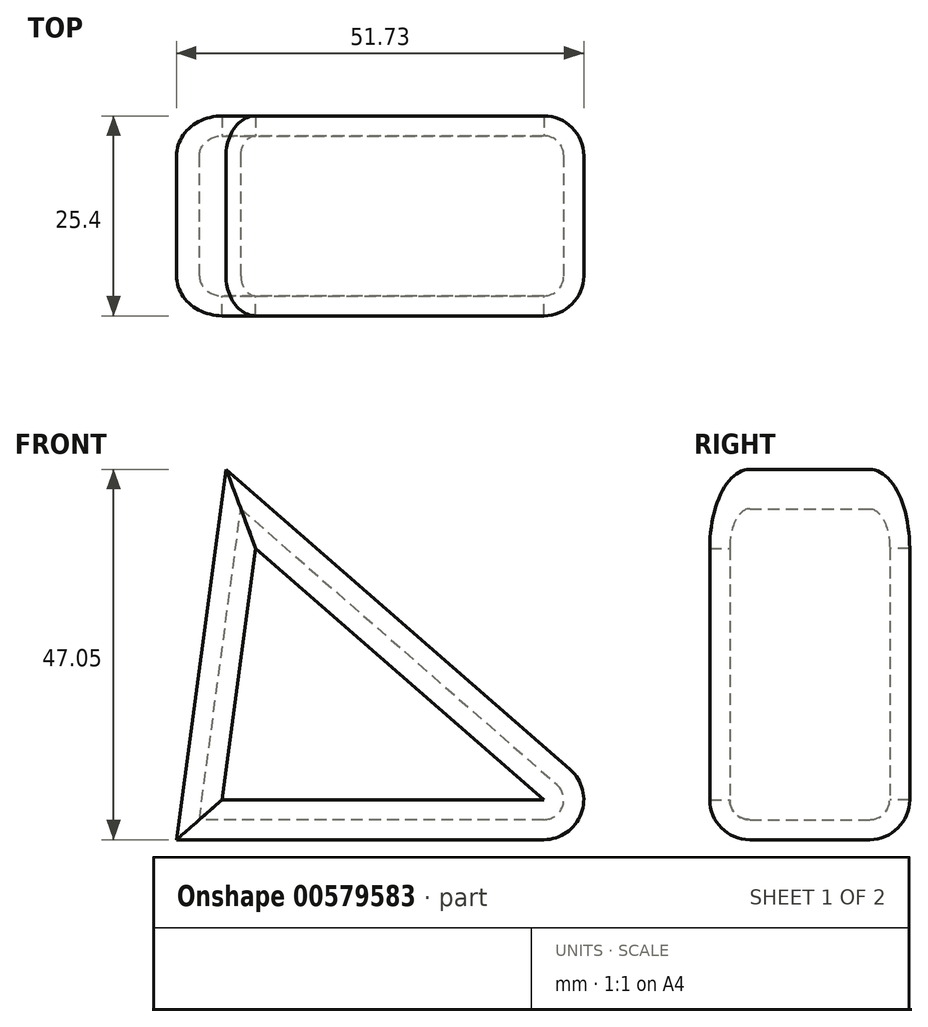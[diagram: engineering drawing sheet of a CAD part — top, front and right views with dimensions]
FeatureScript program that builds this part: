
annotation { "Feature Type Name" : "Feature", "Feature Type Description" : "" }
export const myFeature = defineFeature(function(context is Context, id is Id, definition is map)
    precondition{}
    {
        {
            var Q0;
            Q0=qCreatedBy(makeId("Front.planeOp"),FACE);
            var sketch = newSketch(context, id + "F0", { "sketchPlane" : qUnion([Q0])});
            skLineSegment(sketch, "E0", {"start": v(-18.29, 47.05) * mm, "end": v(35.62, 0) * mm});
            skLineSegment(sketch, "E1", {"start": v(35.62, 0) * mm, "end": v(-24.57, 0) * mm});
            skLineSegment(sketch, "E2", {"start": v(-24.57, 0) * mm, "end": v(-18.29, 47.05) * mm});
            skSolve(sketch);
        }
        {
            var Q0;
            Q0 = qSketchRegion(id + "F0", true);
            extrude(context, id + "F1", {"entities" : qUnion([Q0]), "depth" : 25.4 * mm, "offsetDistance" : 25.4 * mm});
        }
        {
            var Q0;
            Q0=makeQuery(id+"F1.opExtrude","CAP_EDGE",EDGE,{"disambiguationData":[OSD([sQuery(id+"F0.wireOp",EDGE,"E0")])],"isStart":false});
            var Q1;
            Q1=makeQuery(id+"F1.opExtrude","CAP_EDGE",EDGE,{"disambiguationData":[OSD([sQuery(id+"F0.wireOp",EDGE,"E2")])],"isStart":false});
            var Q2;
            Q2=makeQuery(id+"F1.opExtrude","CAP_EDGE",EDGE,{"disambiguationData":[OSD([sQuery(id+"F0.wireOp",EDGE,"E1")])],"isStart":false});
            var Q3;
            Q3=makeQuery(id+"F1.opExtrude","SWEPT_EDGE",EDGE,{"disambiguationData":[OSD([sQuery(id+"F0.wireOp",EDGE,"E0"),sQuery(id+"F0.wireOp",EDGE,"E1")])]});
            var Q4;
            Q4=makeQuery(id+"F1.opExtrude","CAP_EDGE",EDGE,{"disambiguationData":[OSD([sQuery(id+"F0.wireOp",EDGE,"E0")])],"isStart":true});
            var Q5;
            Q5=makeQuery(id+"F1.opExtrude","CAP_EDGE",EDGE,{"disambiguationData":[OSD([sQuery(id+"F0.wireOp",EDGE,"E2")])],"isStart":true});
            var Q6;
            Q6=makeQuery(id+"F1.opExtrude","CAP_EDGE",EDGE,{"disambiguationData":[OSD([sQuery(id+"F0.wireOp",EDGE,"E1")])],"isStart":true});
            fillet(context, id + "F2", {"entities" : qUnion([Q0, Q1, Q2, Q3, Q4, Q5, Q6]), "radius" : 5.08 * mm, "tangentPropagation" : true, "allowEdgeOverflow" : false});
        }
        {
            var Q0;
            Q0=makeQuery(id+"F1.opExtrude","CAP_FACE",FACE,{"disambiguationData":[OSD([sQuery(id+"F0.wireOp",EDGE,"E0"),sQuery(id+"F0.wireOp",EDGE,"E1"),sQuery(id+"F0.wireOp",EDGE,"E2")])],"isStart":true});
            var Q1;
            Q1=makeQuery(id+"F1.opExtrude","CAP_FACE",FACE,{"disambiguationData":[OSD([sQuery(id+"F0.wireOp",EDGE,"E0"),sQuery(id+"F0.wireOp",EDGE,"E1"),sQuery(id+"F0.wireOp",EDGE,"E2")])],"isStart":false});
            shell(context, id + "F3", {"entities" : qUnion([Q0, Q1]), "thickness" : 2.54 * mm});
        }
    });
